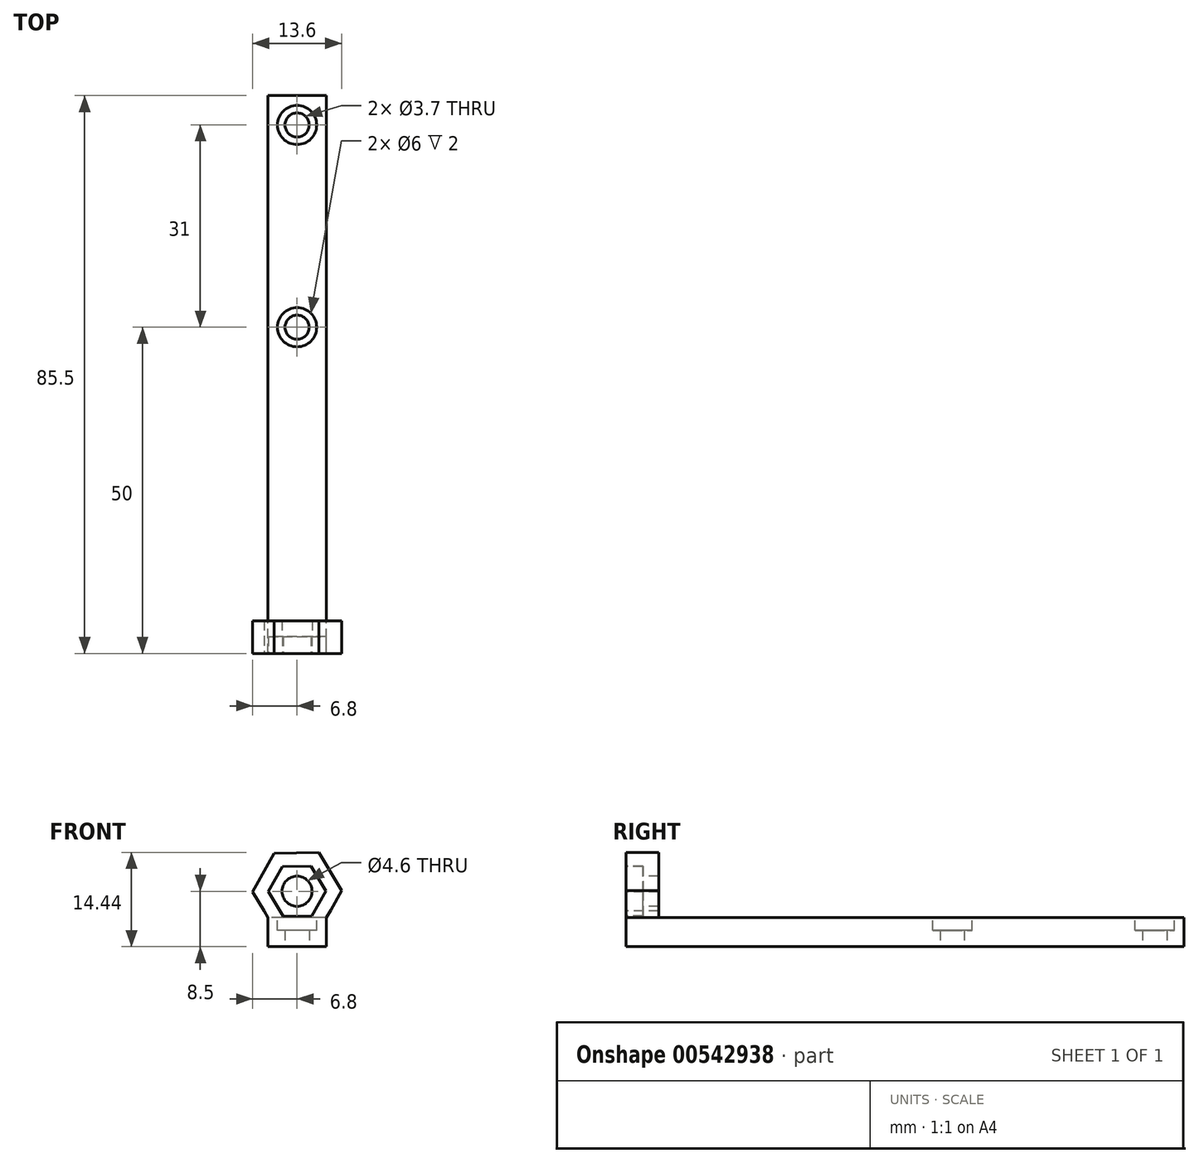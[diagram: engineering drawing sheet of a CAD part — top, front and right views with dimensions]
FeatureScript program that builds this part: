
annotation { "Feature Type Name" : "Feature", "Feature Type Description" : "" }
export const myFeature = defineFeature(function(context is Context, id is Id, definition is map)
    precondition{}
    {
        {
            var Q0;
            Q0=qCreatedBy(makeId("Top.planeOp"),FACE);
            var sketch = newSketch(context, id + "F0", { "sketchPlane" : qUnion([Q0])});
            skLineSegment(sketch, "E0.bottom", {"start": v(4.5, -42.75) * mm, "end": v(-4.5, -42.75) * mm});
            skLineSegment(sketch, "E0.top", {"start": v(4.5, 42.75) * mm, "end": v(-4.5, 42.75) * mm});
            skLineSegment(sketch, "E0.left", {"start": v(4.5, -42.75) * mm, "end": v(4.5, 42.75) * mm});
            skLineSegment(sketch, "E0.right", {"start": v(-4.5, -42.75) * mm, "end": v(-4.5, 42.75) * mm});
            skPoint(sketch, "E0.middle", {"position": v(0, 0) * mm});
            skCircle(sketch, "E1", {"center": v(0, 38.25) * mm, "radius": 1.85 * mm});
            skCircle(sketch, "E2", {"center": v(0, 7.25) * mm, "radius": 1.85 * mm});
            skSolve(sketch);
        }
        {
            var Q0;
            Q0=makeQuery(id+"F0.imprint","IMPRINT",FACE,{"disambiguationData":[TD([[makeQuery(id+"F0.imprint","IMPRINT",EDGE,{"derivedFrom":sQuery(id+"F0.wireOp",EDGE,"E0.bottom")}),-1.0]])]});
            extrude(context, id + "F1", {"entities" : qUnion([Q0]), "depth" : 4.5 * mm, "offsetDistance" : 25 * mm});
        }
        {
            var Q0;
            Q0=makeQuery(id+"F1.opExtrude","SWEPT_FACE",FACE,{"disambiguationData":[OSD([sQuery(id+"F0.wireOp",EDGE,"E0.bottom")])]});
            var sketch = newSketch(context, id + "F2", { "sketchPlane" : qUnion([Q0])});
            skCircle(sketch, "E3", {"center": v(0, 8.5) * mm, "radius": 2.3 * mm});
            skCircle(sketch, "E4.cCircle", {"center": v(0, 8.5) * mm, "radius": 5.89 * mm, "construction": true});
            skLineSegment(sketch, "E4.0", {"start": v(6.8, 8.6) * mm, "end": v(5.14, 5.63) * mm});
            skLineSegment(sketch, "E4.2", {"start": v(-5.05, 5.48) * mm, "end": v(-6.8, 8.4) * mm});
            skLineSegment(sketch, "E4.3", {"start": v(-6.8, 8.4) * mm, "end": v(-3.5, 14.34) * mm});
            skLineSegment(sketch, "E4.4", {"start": v(-3.5, 14.34) * mm, "end": v(3.3, 14.44) * mm});
            skLineSegment(sketch, "E4.5", {"start": v(3.3, 14.44) * mm, "end": v(6.8, 8.6) * mm});
            skPoint(sketch, "E4.0.midPoint", {"position": v(5.14, 5.63) * mm});
            skPoint(sketch, "E5.orphan", {"position": v(3.5, 2.66) * mm});
            skPoint(sketch, "E6.orphan", {"position": v(-3.3, 2.56) * mm});
            skLineSegment(sketch, "E7.0", {"start": v(4.5, 4.5) * mm, "end": v(-4.5, 4.5) * mm});
            skLineSegment(sketch, "E8", {"start": v(-5.05, 5.48) * mm, "end": v(-4.5, 4.5) * mm});
            skLineSegment(sketch, "E9", {"start": v(5.14, 5.63) * mm, "end": v(4.5, 4.5) * mm});
            skSolve(sketch);
        }
        {
            var Q0;
            Q0=makeQuery(id+"F2.imprint","IMPRINT",FACE,{"disambiguationData":[TD([[makeQuery(id+"F2.imprint","IMPRINT",EDGE,{"derivedFrom":sQuery(id+"F2.wireOp",EDGE,"E3")}),-1.0]])]});
            extrude(context, id + "F3", {"entities" : qUnion([Q0]), "operationType" : NewBodyOperationType.ADD, "oppositeDirection" : true, "depth" : 5 * mm, "offsetDistance" : 25 * mm});
        }
        {
            var Q0;
            Q0=makeQuery(id+"F3.boolean.opBoolean","MERGE",FACE,{"derivedFrom":[makeQuery(id+"F1.opExtrude","SWEPT_FACE",FACE,{"disambiguationData":[OSD([sQuery(id+"F0.wireOp",EDGE,"E0.bottom")])]}),makeQuery(id+"F3.opExtrude","CAP_FACE",FACE,{"disambiguationData":[OSD([sQuery(id+"F2.wireOp",EDGE,"E3"),sQuery(id+"F2.wireOp",EDGE,"E4.0"),sQuery(id+"F2.wireOp",EDGE,"E4.2"),sQuery(id+"F2.wireOp",EDGE,"E4.3"),sQuery(id+"F2.wireOp",EDGE,"E4.4"),sQuery(id+"F2.wireOp",EDGE,"E4.5"),sQuery(id+"F2.wireOp",EDGE,"E7.0"),sQuery(id+"F2.wireOp",EDGE,"E8"),sQuery(id+"F2.wireOp",EDGE,"E9")])],"isStart":true})]});
            var sketch = newSketch(context, id + "F4", { "sketchPlane" : qUnion([Q0])});
            skCircle(sketch, "E10.cCircle", {"center": v(0, 8.5) * mm, "radius": 3.8 * mm, "construction": true});
            skLineSegment(sketch, "E10.0", {"start": v(2.14, 12.33) * mm, "end": v(4.39, 8.56) * mm});
            skLineSegment(sketch, "E10.1", {"start": v(4.39, 8.56) * mm, "end": v(2.25, 4.73) * mm});
            skLineSegment(sketch, "E10.2", {"start": v(2.25, 4.73) * mm, "end": v(-2.14, 4.67) * mm});
            skLineSegment(sketch, "E10.3", {"start": v(-2.14, 4.67) * mm, "end": v(-4.39, 8.44) * mm});
            skLineSegment(sketch, "E10.4", {"start": v(-4.39, 8.44) * mm, "end": v(-2.25, 12.27) * mm});
            skLineSegment(sketch, "E10.5", {"start": v(-2.25, 12.27) * mm, "end": v(2.14, 12.33) * mm});
            skPoint(sketch, "E10.0.midPoint", {"position": v(3.26, 10.44) * mm});
            skSolve(sketch);
        }
        {
            var Q0;
            Q0=makeQuery(id+"F4.imprint","IMPRINT",FACE,{"disambiguationData":[TD([[makeQuery(id+"F4.imprint","IMPRINT",EDGE,{"derivedFrom":sQuery(id+"F4.wireOp",EDGE,"E10.0")}),-1.0]])]});
            extrude(context, id + "F5", {"entities" : qUnion([Q0]), "operationType" : NewBodyOperationType.REMOVE, "oppositeDirection" : true, "depth" : 2.6 * mm, "offsetDistance" : 25 * mm});
        }
        {
            var Q0;
            Q0=makeQuery(id+"F1.opExtrude","CAP_FACE",FACE,{"disambiguationData":[OSD([sQuery(id+"F0.wireOp",EDGE,"E0.bottom"),sQuery(id+"F0.wireOp",EDGE,"E0.top"),sQuery(id+"F0.wireOp",EDGE,"E0.left"),sQuery(id+"F0.wireOp",EDGE,"E0.right"),sQuery(id+"F0.wireOp",EDGE,"E1"),sQuery(id+"F0.wireOp",EDGE,"E2")])],"isStart":false});
            var sketch = newSketch(context, id + "F6", { "sketchPlane" : qUnion([Q0])});
            skCircle(sketch, "E11", {"center": v(0, 7.25) * mm, "radius": 3 * mm});
            skCircle(sketch, "E12", {"center": v(0, 38.25) * mm, "radius": 3 * mm});
            skSolve(sketch);
        }
        {
            var Q0;
            Q0=makeQuery(id+"F6.imprint","IMPRINT",FACE,{"disambiguationData":[TD([[makeQuery(id+"F6.imprint","IMPRINT",EDGE,{"derivedFrom":sQuery(id+"F6.wireOp",EDGE,"E12")}),1.0]])]});
            var Q1;
            Q1=makeQuery(id+"F6.imprint","IMPRINT",FACE,{"disambiguationData":[TD([[makeQuery(id+"F6.imprint","IMPRINT",EDGE,{"derivedFrom":sQuery(id+"F6.wireOp",EDGE,"E11")}),1.0]])]});
            extrude(context, id + "F7", {"entities" : qUnion([Q0, Q1]), "operationType" : NewBodyOperationType.REMOVE, "oppositeDirection" : true, "depth" : 2 * mm, "offsetDistance" : 25 * mm});
        }
    });
